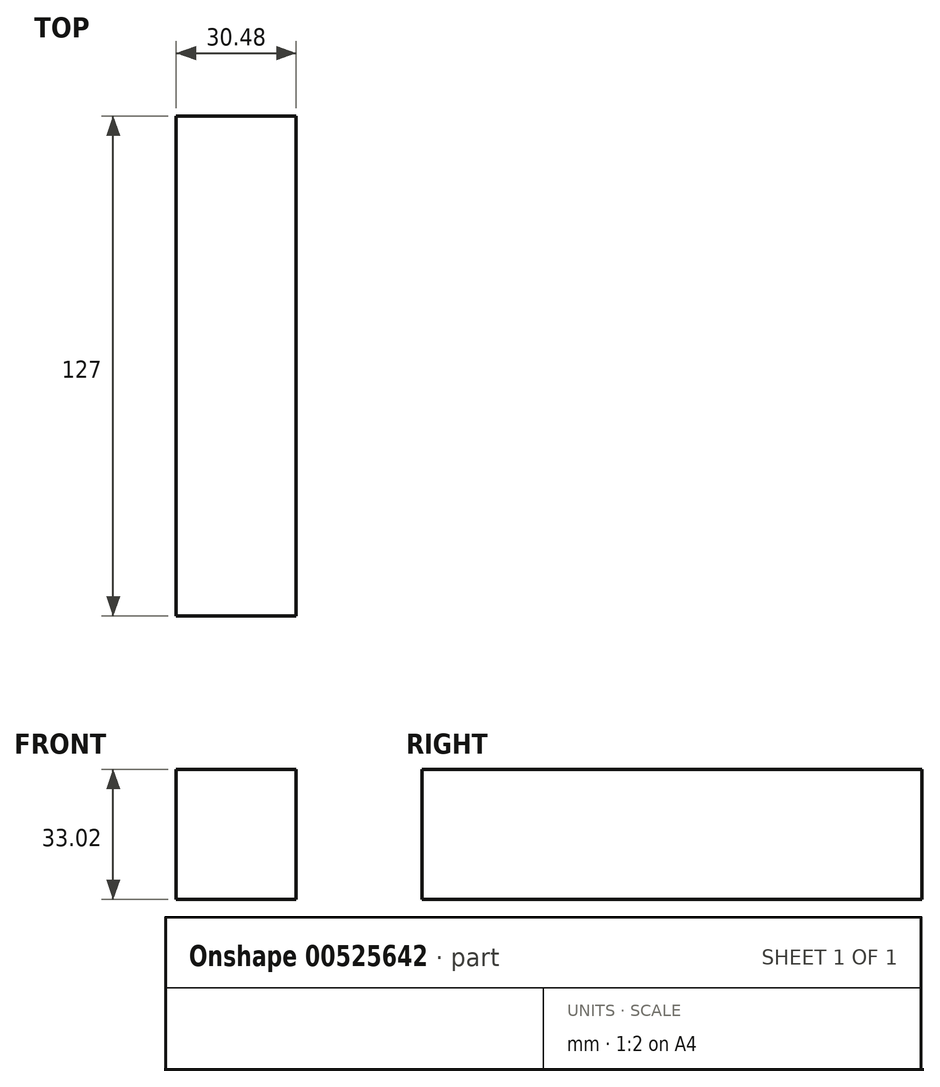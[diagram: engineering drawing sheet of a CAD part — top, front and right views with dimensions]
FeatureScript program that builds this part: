
annotation { "Feature Type Name" : "Feature", "Feature Type Description" : "" }
export const myFeature = defineFeature(function(context is Context, id is Id, definition is map)
    precondition{}
    {
        {
            var Q0;
            Q0=qCreatedBy(makeId("Front.planeOp"),FACE);
            var sketch = newSketch(context, id + "F0", { "sketchPlane" : qUnion([Q0])});
            skLineSegment(sketch, "E0.bottom", {"start": v(0, 0) * mm, "end": v(30.48, 0) * mm});
            skLineSegment(sketch, "E0.top", {"start": v(0, 33.02) * mm, "end": v(30.48, 33.02) * mm});
            skLineSegment(sketch, "E0.left", {"start": v(0, 0) * mm, "end": v(0, 33.02) * mm});
            skLineSegment(sketch, "E0.right", {"start": v(30.48, 0) * mm, "end": v(30.48, 33.02) * mm});
            skSolve(sketch);
        }
        {
            var Q0;
            Q0=makeQuery(id+"F0.imprint","IMPRINT",FACE,{"disambiguationData":[TD([[makeQuery(id+"F0.imprint","IMPRINT",EDGE,{"derivedFrom":sQuery(id+"F0.wireOp",EDGE,"E0.bottom")}),1.0]])]});
            extrude(context, id + "F1", {"entities" : qUnion([Q0]), "depth" : 101.6 * mm, "offsetDistance" : 25.4 * mm});
        }
        {
            var Q0;
            Q0=makeQuery(id+"F1.opExtrude","CAP_FACE",FACE,{"disambiguationData":[OSD([sQuery(id+"F0.wireOp",EDGE,"E0.bottom"),sQuery(id+"F0.wireOp",EDGE,"E0.top"),sQuery(id+"F0.wireOp",EDGE,"E0.left"),sQuery(id+"F0.wireOp",EDGE,"E0.right")])],"isStart":true});
            var sketch = newSketch(context, id + "F2", { "sketchPlane" : qUnion([Q0])});
            skLineSegment(sketch, "E1", {"start": v(-15.24, 33.02) * mm, "end": v(0, 19.17) * mm});
            skSolve(sketch);
        }
        {
            var Q0;
            {var subQ2=sQuery(id+"F2.wireOp",EDGE,"E1");Q0=makeQuery(id+"F2.imprint","IMPRINT",FACE,{"disambiguationData":[TD([[makeQuery(id+"F2.imprint","IMPRINT",EDGE,{"derivedFrom":subQ2}),-1.0]])]});}
            var sketch = newSketch(context, id + "F3", { "sketchPlane" : qUnion([Q0])});
            skLineSegment(sketch, "E2.bottom", {"start": v(0, 0) * mm, "end": v(-30.48, 0) * mm});
            skLineSegment(sketch, "E2.top", {"start": v(0, 33.02) * mm, "end": v(-30.48, 33.02) * mm});
            skLineSegment(sketch, "E2.left", {"start": v(0, 0) * mm, "end": v(0, 33.02) * mm});
            skLineSegment(sketch, "E2.right", {"start": v(-30.48, 0) * mm, "end": v(-30.48, 33.02) * mm});
            skSolve(sketch);
        }
        {
            var Q0;
            Q0 = qSketchRegion(id + "F3", true);
            extrude(context, id + "F4", {"entities" : qUnion([Q0]), "operationType" : NewBodyOperationType.ADD, "depth" : 25.4 * mm, "offsetDistance" : 25.4 * mm});
        }
    });
